# Revit family: RN 84219 Optiflex-Flowpress-Gomito doppio
name_source: partatom
category: Rohrzubehör
units: mm (PartAtom-declared; Revit-internal decimal feet)

## family parameters
Arbeitsebenenbasiert = Nein
Beim Laden mit Abzugskörper schneiden = Nein
Bemaßung runder Anschluss = Durchmesser verwenden
Gemeinsam genutzt = Nein
Immer vertikal = Ja
Teiletyp = Nicht definiert

## types (3) — shared parameters
1.010.00.2 Blattnummer der Richtlinie = 29
1.010.00.3 Ausgabedatum (Monat) der Richtlinie = 201308
1.010.00.4 Herstellername = R. Nussbaum AG
1.010.00.5 Revisionsdatum der Datei = 20190521
1.010.00.6 Webadresse des Herstellers = http://www.nussbaum.ch
1.100.00.4 Produktbezeichnung = Versorgung
1.110.00.2 Index = 5
1.110.00.4 Produktbezeichnung = Optiflex
1.960/3L.00.8 Link (URL) = https://www.nussbaum.ch
29.700.00.4 Produktname = Optiflex-F-Doppel-Anschlusswinkel, mit Wandflansch
29.700.00.5 Produktkennung = 2
29.700.00.6 Querschnittsform = 1
29.700.00.7 Nennweitensystem = DN
29.700.00.8 Nenndrucksystem = PN
29.710.02.4 Nenndruck = 10
29.710.02.5 max. zul. Überdruck [hPa] = 1000
29.710.02.7 max. zul. Dauer-Betriebsdruck [hPa] = 1000
29.710.02.9 max. zul. Dauer-Betriebstemperatur [°C] = 70
CONNECTOR0_dZ_00 = 71 mm
CONNECTOR0_dZ_01 = 57 mm
CONNECTOR0_ref_dX = 18 mm
CONNECTOR0_ref_dY = 25 mm  [stored 0.082021 ft]
CONNECTOR0_ref_dZ = 57 mm
CONNECTOR1_DIAMETER_dX_0r = 15 mm  [stored 0.0492126 ft]
CONNECTOR2_dZ_00 = 71 mm
CONNECTOR2_dZ_01 = 57 mm
CONNECTOR2_ref_dX = 18 mm
CONNECTOR2_ref_dY = 25 mm  [stored 0.082021 ft]
CONNECTOR2_ref_dZ = 57 mm
Connector Visibility = Nein
EnclosingSpace Visibility = Nein
Hersteller = R. Nussbaum AG
URL = https://www.nussbaum.ch

## per-type parameters (varying)
| type | 1.800.00.3 TGA-Nummer | 1.800.00.4 Kommentarfeld | 1.810.00.3 Hersteller-Bestellnummer | 1.810.00.4 DATANORM-Nummer | 1.810.00.5 StLB-Nummer | 1.810.00.6 GTIN-Nummer | 29.710.02.10 Formstück-Gewicht [kg] | 29.710.02.3 Benennung | CONNECTOR0_DIAMETER_dZ_0r | CONNECTOR1_dX_00 | CONNECTOR1_dX_01 | CONNECTOR1_ref_dX | CONNECTOR2_DIAMETER_dZ_0r | Modell | R. Nussbaum AG 84219.21 de Visibility | R. Nussbaum AG 84219.22 de Visibility | R. Nussbaum AG 84219.23 de Visibility | Typenkommentare |
| DN=12x12x15 | 01900500000000000000000000000000000000000000000009000000000000000003 | 84219.23, Optiflex-F-Doppel-Anschlusswinkel, mit Wandflansch, DN=12x12x15, L=90, Rp=½ | 84219.23 | 84219.23 | 343.231 | 7612945730428 | 0.404 | Optiflex-F-Doppel-Anschlusswinkel, mit Wandflansch, DN=12x12x15, L=90, Rp=½ | 12 mm  [stored 0.0393701 ft] | 42 mm  [stored 0.137795 ft] | 90 mm | 42 mm  [stored 0.137795 ft] | 42 mm  [stored 0.137795 ft] | 84219.23 | Nein | Nein | Ja | Optiflex-Flowpress-Gomito doppio DN=12x12x15 |
| DN=15x12x12 | 01900500000000000000000000000000000000000000000009000000000000000002 | 84219.22, Optiflex-F-Doppel-Anschlusswinkel, mit Wandflansch, DN=15x12x12, L=75, Rp=½ | 84219.22 | 84219.22 | 343.232 | 7612945730411 | 0.351 | Optiflex-F-Doppel-Anschlusswinkel, mit Wandflansch, DN=15x12x12, L=75, Rp=½ | 15 mm  [stored 0.0492126 ft] | 27 mm | 75 mm | 27 mm | 12 mm  [stored 0.0393701 ft] | 84219.22 | Nein | Ja | Nein | Optiflex-Flowpress-Gomito doppio DN=15x12x12 |
| DN=12x15x12 | 01900500000000000000000000000000000000000000000009000000000000000001 | 84219.21, Optiflex-F-Doppel-Anschlusswinkel, mit Wandflansch, DN=12x15x12, L=75, Rp=½ | 84219.21 | 84219.21 | 343.231 | 7612945730404 | 0.346 | Optiflex-F-Doppel-Anschlusswinkel, mit Wandflansch, DN=12x15x12, L=75, Rp=½ | 12 mm  [stored 0.0393701 ft] | 27 mm | 75 mm | 27 mm | 12 mm  [stored 0.0393701 ft] | 84219.21 | Ja | Nein | Nein | Optiflex-Flowpress-Gomito doppio DN=12x15x12 |

note: [stored X ft] marks values corroborated as IEEE doubles in the binary element streams (Revit-internal decimal feet)

## geometry (parser evidence)
native form markers: Sweep x1
no freeform markers — native parametric forms only
